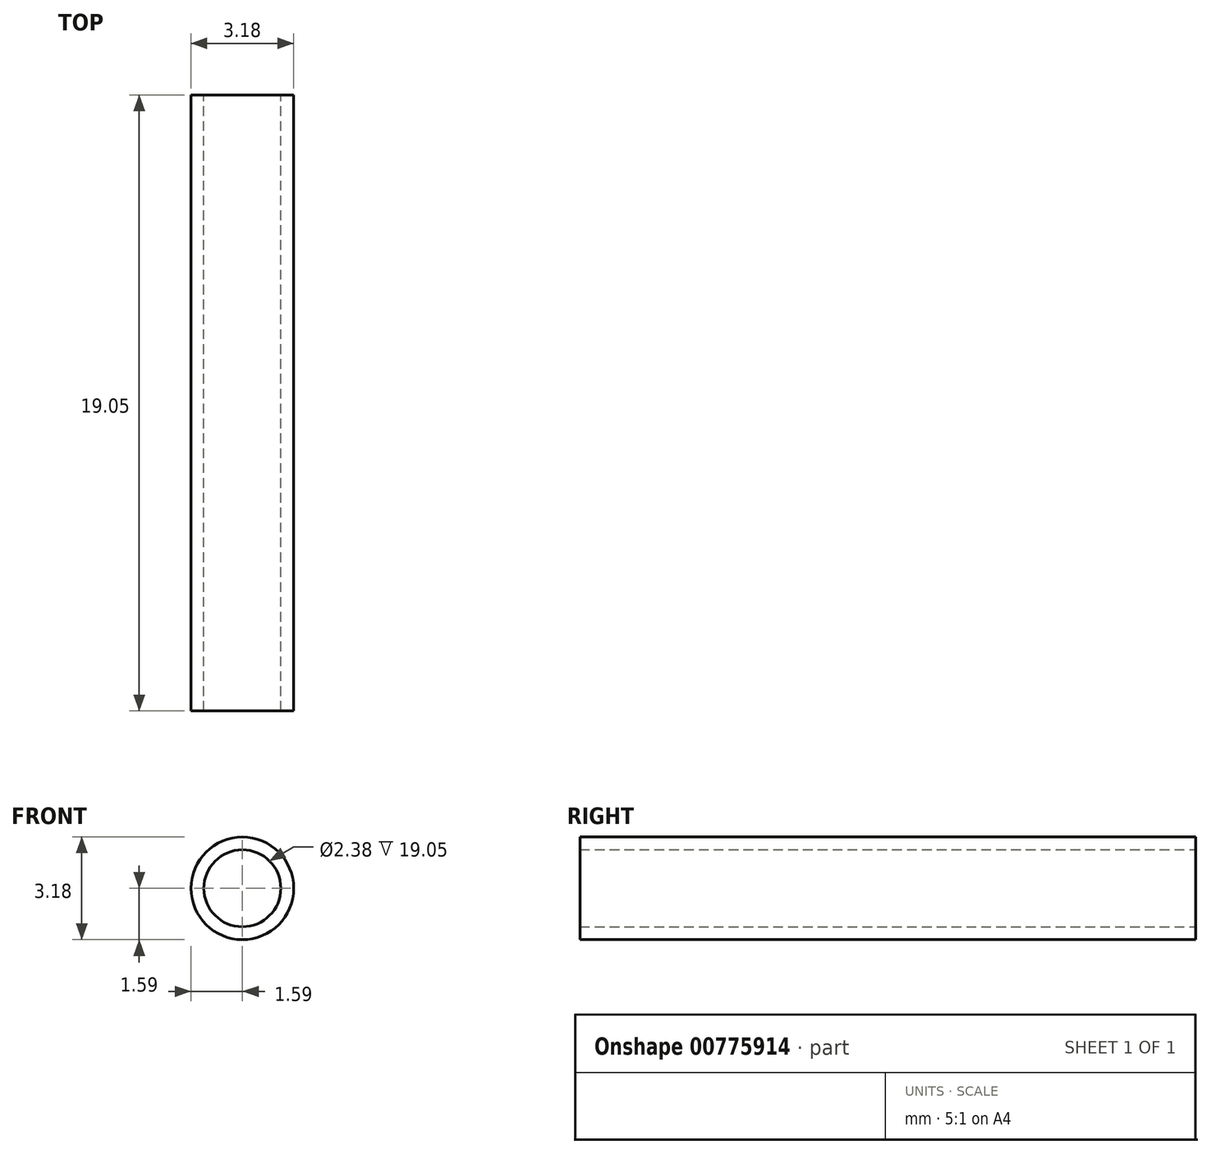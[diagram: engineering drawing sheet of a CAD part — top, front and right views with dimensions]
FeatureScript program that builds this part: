
annotation { "Feature Type Name" : "Feature", "Feature Type Description" : "" }
export const myFeature = defineFeature(function(context is Context, id is Id, definition is map)
    precondition{}
    {
        {
            var Q0;
            Q0=qCreatedBy(makeId("Front.planeOp"),FACE);
            var sketch = newSketch(context, id + "F0", { "sketchPlane" : qUnion([Q0])});
            skCircle(sketch, "E0", {"center": v(0, 0) * mm, "radius": 1.2 * mm});
            skArc(sketch, "E1", {"start": v(1.54, 0.4) * mm, "mid": v(0, 1.59) * mm, "end": v(-1.54, 0.4) * mm});
            skLineSegment(sketch, "E2.bottom", {"start": v(1.59, -0.4) * mm, "end": v(1.54, -0.4) * mm});
            skLineSegment(sketch, "E2.top", {"start": v(1.59, 0.4) * mm, "end": v(1.54, 0.4) * mm});
            skLineSegment(sketch, "E2.left", {"start": v(1.59, -0.4) * mm, "end": v(1.59, 0.4) * mm});
            skLineSegment(sketch, "E3.MirrorCS", {"start": v(-1.59, 0.4) * mm, "end": v(-1.54, 0.4) * mm});
            skLineSegment(sketch, "E4.MirrorCS", {"start": v(-1.59, -0.4) * mm, "end": v(-1.59, 0.4) * mm});
            skLineSegment(sketch, "E5.MirrorCS", {"start": v(-1.59, -0.4) * mm, "end": v(-1.54, -0.4) * mm});
            skArc(sketch, "E6.trimOffspring", {"start": v(-1.54, -0.4) * mm, "mid": v(0, -1.59) * mm, "end": v(1.54, -0.4) * mm});
            skCircle(sketch, "E7", {"center": v(0, 0) * mm, "radius": 1.59 * mm});
            skSolve(sketch);
        }
        {
            var Q0;
            Q0=makeQuery(id+"F0.imprint","IMPRINT",FACE,{"disambiguationData":[TD([[makeQuery(id+"F0.imprint","IMPRINT",EDGE,{"derivedFrom":sQuery(id+"F0.wireOp",EDGE,"E0")}),-1.0]])]});
            extrude(context, id + "F1", {"entities" : qUnion([Q0]), "depth" : 19.05 * mm, "offsetDistance" : 25.4 * mm});
        }
    });
